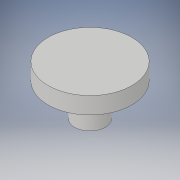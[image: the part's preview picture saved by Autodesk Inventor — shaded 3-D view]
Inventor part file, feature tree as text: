
AUTODESK INVENTOR PART (.ipt)
format: ipt  version: 2019.4 (Build 234330000, 330)  size: 116,224 bytes
history: native  units: in
note: dims shown in document units (in); Inventor stores cm internally (conversion verified against a paired STEP export)
features: sketch x3, extrude x2, hole x1
ambient origin geometry x8: Origin, YZ Plane, XZ Plane, XY Plane, X Axis, Y Axis, Z Axis, Center Point
bodies: Solid1 (feature_tree)
feature tree (6):
  extrude  "Extrusion1"  Depth=0.412in TaperAngle=0.0deg
  extrude  "Extrusion2"  Depth=0.8in TaperAngle=0.0deg
  hole  "Hole1"  [1 undecoded]
  sketch  "Sketch1"  dims[d0=2.05in d1=0.412in d2=0.0in]
  sketch  "Sketch2"  dims[d3=0.75in d4=0.8in d5=0.0in]
  sketch  "Sketch3"  dims[d6=0.1575in d7=0.1575in d8=0.1181in d9=0.157in d10=0.157in d11=0.1875in d12=0.75in d13=0.375in d14=0.25in d15=0.5635in d16=0.5in d17=0.8108in]
note: 1 required parameter value undecoded (feature->parameter linkage not recoverable at this tier; creation-order binding heuristic only, values carry confidence <= 0.55)
